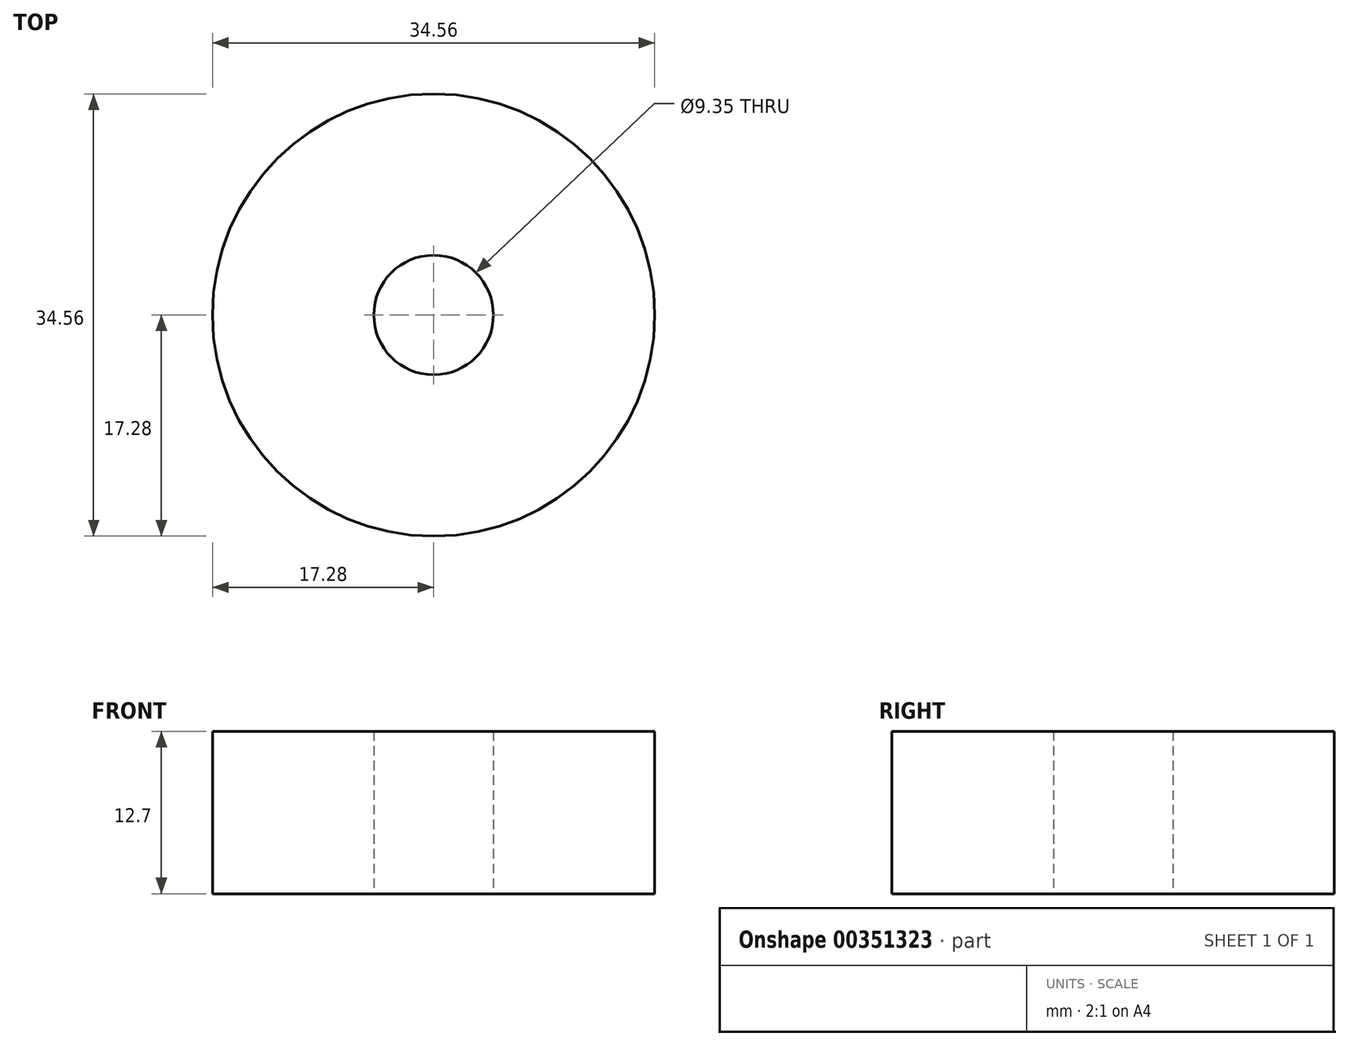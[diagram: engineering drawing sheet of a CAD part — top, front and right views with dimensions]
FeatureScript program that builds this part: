
annotation { "Feature Type Name" : "Feature", "Feature Type Description" : "" }
export const myFeature = defineFeature(function(context is Context, id is Id, definition is map)
    precondition{}
    {
        {
            var Q0;
            Q0=qCreatedBy(makeId("Top.planeOp"),FACE);
            var sketch = newSketch(context, id + "F0", { "sketchPlane" : qUnion([Q0])});
            skCircle(sketch, "E0", {"center": v(0, 0) * mm, "radius": 17.28 * mm});
            skCircle(sketch, "E1", {"center": v(0, 0) * mm, "radius": 4.67 * mm});
            skSolve(sketch);
        }
        {
            var Q0;
            Q0 = qSketchRegion(id + "F0", true);
            extrude(context, id + "F1", {"entities" : qUnion([Q0]), "depth" : 12.7 * mm});
        }
    });
